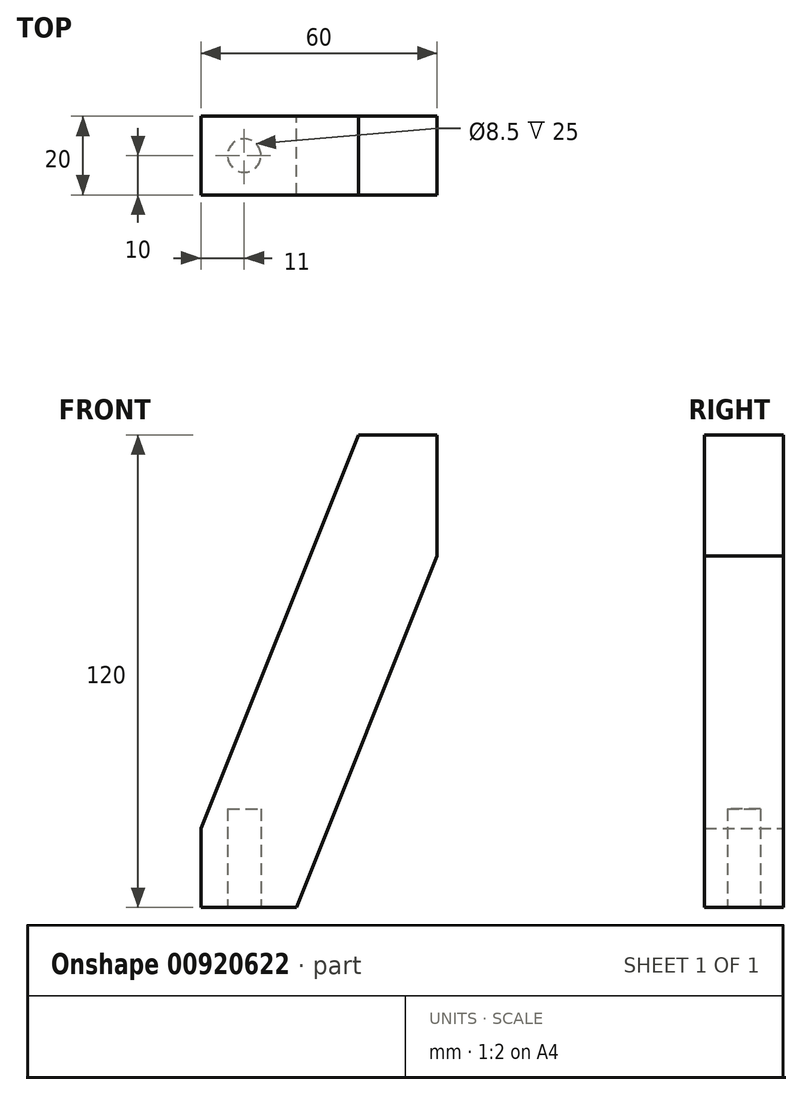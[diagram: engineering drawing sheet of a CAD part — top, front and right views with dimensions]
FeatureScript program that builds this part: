
annotation { "Feature Type Name" : "Feature", "Feature Type Description" : "" }
export const myFeature = defineFeature(function(context is Context, id is Id, definition is map)
    precondition{}
    {
        {
            var Q0;
            Q0=qCreatedBy(makeId("Front.planeOp"),FACE);
            var sketch = newSketch(context, id + "F0", { "sketchPlane" : qUnion([Q0])});
            skLineSegment(sketch, "E0", {"start": v(-60, 0) * mm, "end": v(-35.69, 0) * mm});
            skLineSegment(sketch, "E1", {"start": v(0, 89.22) * mm, "end": v(0, 120) * mm});
            skLineSegment(sketch, "E2", {"start": v(0, 120) * mm, "end": v(-20, 120) * mm});
            skLineSegment(sketch, "E3", {"start": v(-20, 120) * mm, "end": v(-60, 20) * mm});
            skLineSegment(sketch, "E4", {"start": v(-60, 20) * mm, "end": v(-60, 0) * mm});
            skLineSegment(sketch, "E5", {"start": v(0, 89.22) * mm, "end": v(-35.69, 0) * mm});
            skPoint(sketch, "E6.end.orphan", {"position": v(0, 60) * mm});
            skSolve(sketch);
        }
        {
            var Q0;
            Q0=makeQuery(id+"F0.imprint","IMPRINT",FACE,{"disambiguationData":[TD([[makeQuery(id+"F0.imprint","IMPRINT",EDGE,{"derivedFrom":sQuery(id+"F0.wireOp",EDGE,"E0")}),1.0]])]});
            extrude(context, id + "F1", {"entities" : qUnion([Q0]), "depth" : 20 * mm, "offsetDistance" : 25 * mm, "symmetric" : true});
        }
        {
            var Q0;
            Q0=makeQuery(id+"F1.opExtrude","SWEPT_FACE",FACE,{"disambiguationData":[OSD([sQuery(id+"F0.wireOp",EDGE,"E0")])]});
            var sketch = newSketch(context, id + "F2", { "sketchPlane" : qUnion([Q0])});
            skCircle(sketch, "E7", {"center": v(-49, 0) * mm, "radius": 4.25 * mm});
            skSolve(sketch);
        }
        {
            var Q0;
            Q0=makeQuery(id+"F2.imprint","IMPRINT",FACE,{"disambiguationData":[TD([[makeQuery(id+"F2.imprint","IMPRINT",EDGE,{"derivedFrom":sQuery(id+"F2.wireOp",EDGE,"E7")}),1.0]])]});
            extrude(context, id + "F3", {"entities" : qUnion([Q0]), "operationType" : NewBodyOperationType.REMOVE, "oppositeDirection" : true, "depth" : 25 * mm, "offsetDistance" : 25 * mm});
        }
    });
